# Revit family: UOKR124-SS01A
name_source: partatom
category: Furniture
revit_build: Autodesk Revit 2017 (Build: 20160225_1515(x64)
units: mm (PartAtom-declared; Revit-internal decimal feet)

## family parameters
Always vertical = Yes
Cut with Voids When Loaded = No
OmniClass Number = 23.40.20.00
OmniClass Title = General Furniture and Specialties
Room Calculation Point = No
Shared = No
Work Plane-Based = No

## types (1)
- UOKR124-SS01A
    Description = Convection cooling system provides a quick cool down and
consistent temperature
    Dimensions = 34 1/8"H x 23 15/16"W x 22 1/2"D
    Door Swing = Field Reversible
    Finish = Stainless Steel-Satin Brushed
    Lock = No
    Manufacturer = U-LINE
    Model = UOKR124-SS01A
    Pump = No
    Shipping Weight = 117 lb
    Type Comments = Volume of 4.7 cu ft can fit up to one 1⁄4 slim barrel and one 1⁄6
barrel or one standard 1⁄4 barrel
    URL = www.yepsketch.com
    Voltage/Hz = 115/60

## geometry (parser evidence)
native form markers: Sweep x8
no freeform markers — native parametric forms only
